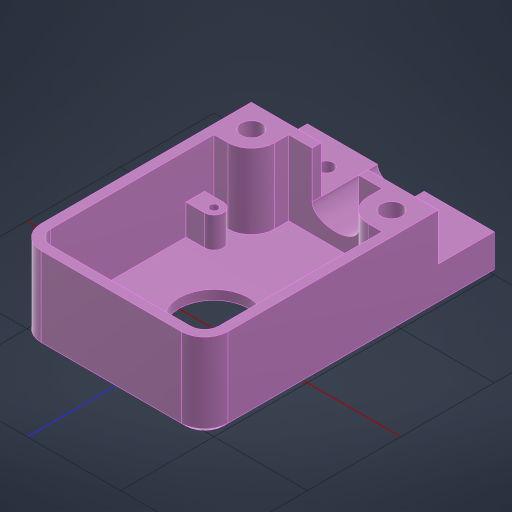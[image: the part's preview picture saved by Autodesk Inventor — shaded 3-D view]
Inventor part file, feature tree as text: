
AUTODESK INVENTOR PART (.ipt)
format: ipt  version: 2023.2 (Build 272271030, 271C)  size: 345,088 bytes
history: native  units: mm
features: extrude x6, sketch x3, projected_geometry x3, hole x1, chamfer x1
ambient origin geometry x8: Origin, YZ Plane, XZ Plane, XY Plane, X Axis, Y Axis, Z Axis, Center Point
bodies: Volumenkörper1 (feature_tree)
feature tree (14):
  sketch  "Skizze1"  dims[d2=15.0mm d3=40.0mm]
  extrude  "Extrusion1"  Depth=40.0mm
  extrude  "Extrusion2"  Depth=5.0mm
  extrude  "Extrusion3"  Depth=28.0mm
  extrude  "Extrusion4"  Depth=2.0mm TaperAngle=0.0deg
  hole  "Bohrung1"  [1 undecoded]
  extrude  "Extrusion5"  Depth=16.0mm TaperAngle=0.0deg
  extrude  "Extrusion6"  Depth=6.0mm TaperAngle=0.0deg
  chamfer  "Fase1"  Distance=6.5mm
  sketch  "Skizze2"  dims[d5=22.0mm d7=5.0mm]
  projected_geometry  "Projizierte Kontur1"
  sketch  "Skizze3"  dims[d10=2.0mm d14=1.8mm d15=2.0mm d16=0.0mm d18=2.0mm d19=16.0mm d20=0.0mm d21=6.0mm d22=0.0mm d23=6.5mm d24=0.0mm d25=20.0mm d26=6.0mm d27=3.2mm d28=6.0mm d29=6.5mm d30=3.4mm d31=14.3117mm d32=8.0mm d33=20.594885mm d34=1.0mm d35=2.0mm d36=45.0deg d37=3.0mm d38=5.0mm d39=10.0mm d40=0.0mm d41=12.0mm d42=2.0mm d43=2.0mm d44=26.0mm d45=4.5mm d47=10.0mm d48=0.0mm d49=10.0mm d50=28.0mm d51=2.0mm d52=28.0mm]
  projected_geometry  "Projizierte Kontur2"
  projected_geometry  "Projizierte Kontur3"
note: 1 required parameter value undecoded (feature->parameter linkage not recoverable at this tier; creation-order binding heuristic only, values carry confidence <= 0.55)
